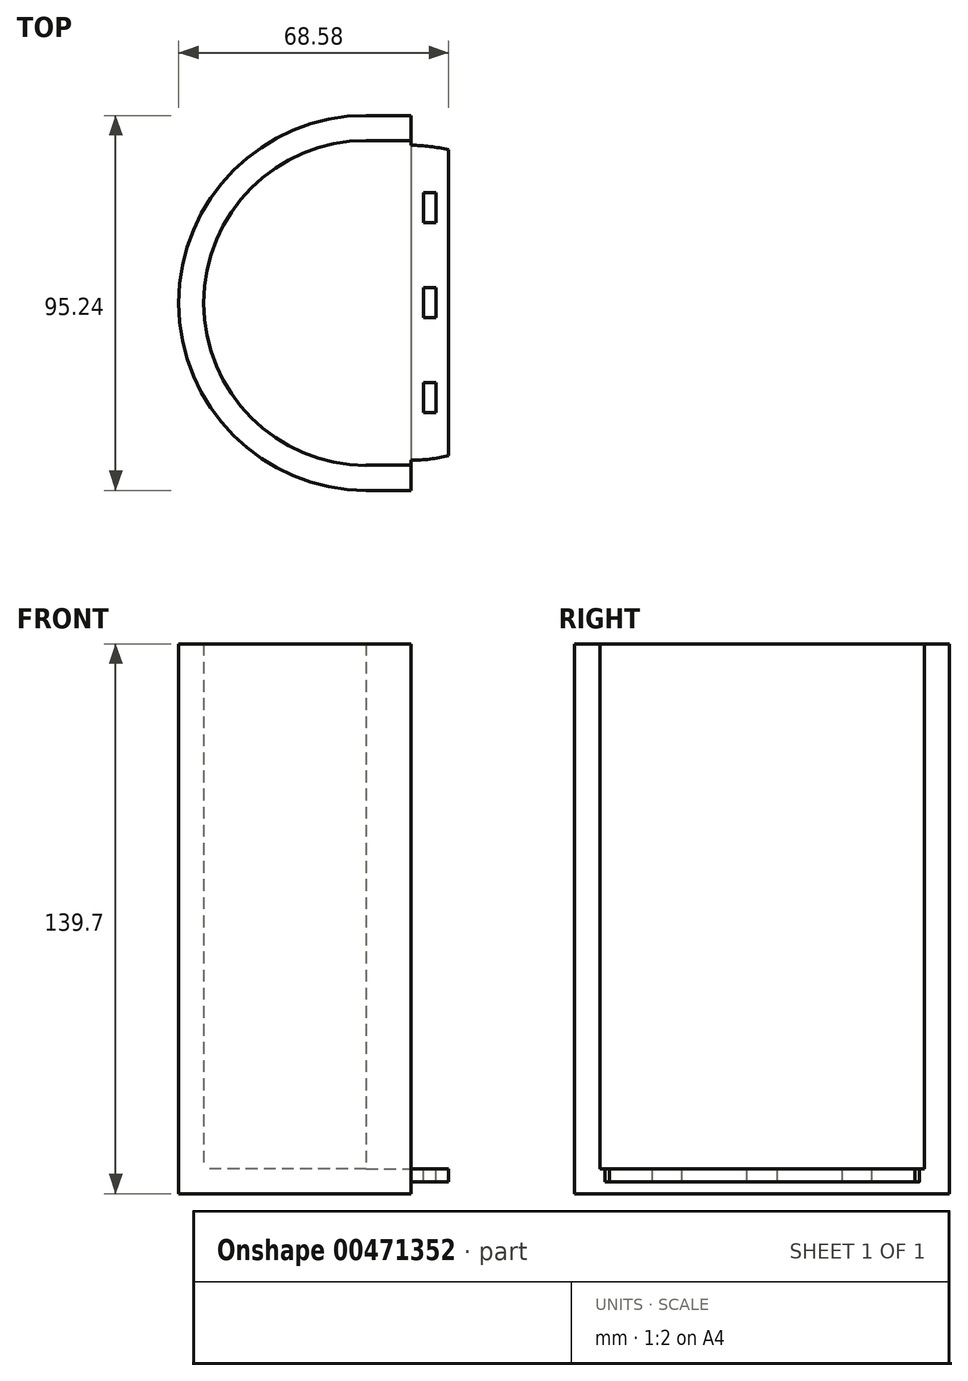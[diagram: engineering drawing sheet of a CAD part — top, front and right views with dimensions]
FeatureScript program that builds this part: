
annotation { "Feature Type Name" : "Feature", "Feature Type Description" : "" }
export const myFeature = defineFeature(function(context is Context, id is Id, definition is map)
    precondition{}
    {
        {
            var Q0;
            Q0=qCreatedBy(makeId("Top.planeOp"),FACE);
            var sketch = newSketch(context, id + "F0", { "sketchPlane" : qUnion([Q0])});
            skArc(sketch, "E0", {"start": v(0, 47.63) * mm, "mid": v(-47.63, 0) * mm, "end": v(0, -47.63) * mm});
            skArc(sketch, "E1", {"start": v(0, 41.28) * mm, "mid": v(-41.28, 0) * mm, "end": v(0, -41.28) * mm});
            skLineSegment(sketch, "E2.bottom", {"start": v(-47.96, 0) * mm, "end": v(-47.95, 0) * mm});
            skLineSegment(sketch, "E2.top", {"start": v(-47.96, -5.19) * mm, "end": v(-47.95, -5.19) * mm});
            skLineSegment(sketch, "E3.trimOffspring", {"start": v(0, -41.23) * mm, "end": v(0, -41.28) * mm});
            skLineSegment(sketch, "E4.bottom", {"start": v(0, 47.63) * mm, "end": v(11.43, 47.63) * mm});
            skLineSegment(sketch, "E4.top", {"start": v(0, 41.2) * mm, "end": v(11.43, 41.2) * mm});
            skLineSegment(sketch, "E4.left", {"start": v(0, 41.28) * mm, "end": v(0, 41.2) * mm});
            skLineSegment(sketch, "E4.right", {"start": v(11.43, 47.63) * mm, "end": v(11.43, 41.2) * mm});
            skLineSegment(sketch, "E5.bottom", {"start": v(0, -47.63) * mm, "end": v(11.43, -47.63) * mm});
            skLineSegment(sketch, "E5.top", {"start": v(0, -41.23) * mm, "end": v(11.43, -41.23) * mm});
            skLineSegment(sketch, "E5.right", {"start": v(11.43, -47.63) * mm, "end": v(11.43, -41.23) * mm});
            skSolve(sketch);
        }
        {
            var Q0;
            Q0 = qSketchRegion(id + "F0", true);
            extrude(context, id + "F1", {"entities" : qUnion([Q0]), "depth" : 133.35 * mm, "offsetDistance" : 25.4 * mm});
        }
        {
            var Q0;
            Q0=qCreatedBy(makeId("Top.planeOp"),FACE);
            var sketch = newSketch(context, id + "F2", { "sketchPlane" : qUnion([Q0])});
            skArc(sketch, "E6", {"start": v(0, 47.63) * mm, "mid": v(-47.63, 0) * mm, "end": v(0, -47.63) * mm});
            skLineSegment(sketch, "E7", {"start": v(0, -47.63) * mm, "end": v(0, 47.63) * mm});
            skLineSegment(sketch, "E8.bottom", {"start": v(0, 47.63) * mm, "end": v(11.43, 47.63) * mm});
            skLineSegment(sketch, "E8.top", {"start": v(0, -47.63) * mm, "end": v(11.43, -47.63) * mm});
            skLineSegment(sketch, "E8.right", {"start": v(11.43, 47.63) * mm, "end": v(11.43, -47.63) * mm});
            skSolve(sketch);
        }
        {
            var Q0;
            Q0 = qSketchRegion(id + "F2", true);
            extrude(context, id + "F3", {"entities" : qUnion([Q0]), "operationType" : NewBodyOperationType.ADD, "oppositeDirection" : true, "depth" : 6.35 * mm, "offsetDistance" : 25.4 * mm});
        }
        {
            var Q0;
            Q0=makeQuery(id+"F3.opExtrude","CAP_FACE",FACE,{"disambiguationData":[OSD([sQuery(id+"F2.wireOp",EDGE,"E6"),sQuery(id+"F2.wireOp",EDGE,"E7")])],"isStart":true});
            var sketch = newSketch(context, id + "F4", { "sketchPlane" : qUnion([Q0])});
            skLineSegment(sketch, "E9", {"start": v(11.43, 40.04) * mm, "end": v(11.43, -39.97) * mm});
            skLineSegment(sketch, "E10", {"start": v(20.96, 38.9) * mm, "end": v(20.96, -38.82) * mm});
            skLineSegment(sketch, "E11.bottom", {"start": v(17.78, 3.85) * mm, "end": v(14.6, 3.85) * mm});
            skLineSegment(sketch, "E11.top", {"start": v(17.78, -3.77) * mm, "end": v(14.6, -3.77) * mm});
            skLineSegment(sketch, "E11.left", {"start": v(17.78, 3.85) * mm, "end": v(17.78, -3.77) * mm});
            skLineSegment(sketch, "E11.right", {"start": v(14.6, 3.85) * mm, "end": v(14.6, -3.77) * mm});
            skPoint(sketch, "E11.middle", {"position": v(16.2, 0.04) * mm});
            skArc(sketch, "E12", {"start": v(11.43, -39.97) * mm, "mid": v(16.23, -39.68) * mm, "end": v(20.96, -38.82) * mm});
            skArc(sketch, "E13.trimOffspring", {"start": v(20.96, 38.9) * mm, "mid": v(16.23, 39.75) * mm, "end": v(11.43, 40.04) * mm});
            skLineSegment(sketch, "E14.bottom", {"start": v(14.62, -27.9) * mm, "end": v(17.8, -27.9) * mm});
            skLineSegment(sketch, "E14.top", {"start": v(14.62, -20.28) * mm, "end": v(17.8, -20.28) * mm});
            skLineSegment(sketch, "E14.left", {"start": v(14.62, -27.9) * mm, "end": v(14.62, -20.28) * mm});
            skLineSegment(sketch, "E14.right", {"start": v(17.8, -27.9) * mm, "end": v(17.8, -20.28) * mm});
            skLineSegment(sketch, "E15.bottom", {"start": v(14.62, 20.36) * mm, "end": v(17.8, 20.36) * mm});
            skLineSegment(sketch, "E15.top", {"start": v(14.62, 27.98) * mm, "end": v(17.8, 27.98) * mm});
            skLineSegment(sketch, "E15.left", {"start": v(14.62, 20.36) * mm, "end": v(14.62, 27.98) * mm});
            skLineSegment(sketch, "E15.right", {"start": v(17.8, 20.36) * mm, "end": v(17.8, 27.98) * mm});
            skSolve(sketch);
        }
        {
            var Q0;
            Q0=makeQuery(id+"F4.imprint","IMPRINT",FACE,{"disambiguationData":[TD([[makeQuery(id+"F4.imprint","IMPRINT",EDGE,{"derivedFrom":sQuery(id+"F4.wireOp",EDGE,"E9")}),1.0]])]});
            extrude(context, id + "F5", {"entities" : qUnion([Q0]), "operationType" : NewBodyOperationType.ADD, "oppositeDirection" : true, "depth" : 3.3 * mm, "offsetDistance" : 25.4 * mm});
        }
    });
